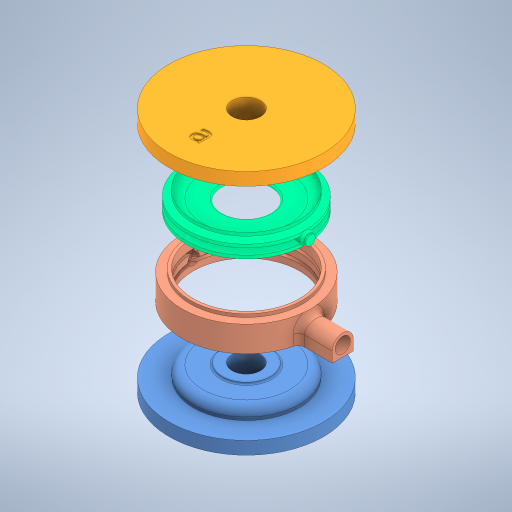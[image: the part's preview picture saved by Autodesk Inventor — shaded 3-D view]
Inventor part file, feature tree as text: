
AUTODESK INVENTOR PART (.ipt)
format: ipt  version: 2023.3 (Build 273359000, 359)  size: 1,031,680 bytes
history: native  units: mm
features: other x12, sketch x6, extrude x6, move_body x6, boolean_combine x4, thicken_offset x4, emboss x2, projected_geometry x2, direct_edit x1
ambient origin geometry x8: Origin, YZ Plane, XZ Plane, XY Plane, X Axis, Y Axis, Z Axis, Center Point
bodies: Solid3 (feature_tree), Solid4 (feature_tree), Solid8 (feature_tree), Solid9 (feature_tree), Solid1 (feature_tree), Solid1_1 (feature_tree), Solid1_2 (feature_tree), Solid1_3 (feature_tree), Solid1_4 (feature_tree)
feature tree (43):
  other  "Sealingring_holder.ipt"
  other  "Sealingring.ipt"
  sketch  "Sketch1"  dims[d0=10.0mm d1=10.0mm]
  extrude  "Extrusion1"  Depth=10.0mm
  boolean_combine  "Combine1"
  sketch  "Sketch2"  dims[d2=8.0mm d3=0.0mm d4=8.8mm]
  extrude  "Extrusion2"  Depth=8.8mm
  thicken_offset  "Thicken1"
  extrude  "Extrusion3"  Depth=0.1mm
  boolean_combine  "Combine2"
  extrude  "Extrusion4"  Depth=8.0mm TaperAngle=0.0deg
  thicken_offset  "Thicken2"
  thicken_offset  "Thicken3"
  thicken_offset  "Thicken4"
  emboss  "Emboss1"
  emboss  "Emboss2"
  extrude  "Extrusion5"  Depth=10.0mm
  boolean_combine  "Combine3"
  extrude  "Extrusion6"  Depth=10.0mm
  boolean_combine  "Combine4"
  direct_edit  "Direct Edit1"
  other  "Solid1::Sealingring_holder.ipt"
  other  "TaggingFeature1"
  other  "Solid1::Sealingring.ipt"
  other  "TaggingFeature2"
  other  "Solid1::Sealingring_holder.ipt_1"
  other  "TaggingFeature3"
  other  "Solid1::Sealingring.ipt_1"
  other  "TaggingFeature4"
  sketch  "Sketch3"  dims[d5=1.5mm d6=0.0mm d7=0.1mm]
  sketch  "Sketch4"  dims[d8=0.1mm d9=8.0mm d10=0.0mm]
  other  "Solid1::Sealingring_holder.ipt_2"
  other  "TaggingFeature5"
  sketch  "Sketch5"  dims[d11=10.0mm d12=10.0mm]
  projected_geometry  "Projected Loop1"
  projected_geometry  "Projected Loop2"
  sketch  "Sketch6"  dims[d13=3.0mm d14=-1.22173mm d15=0.341181mm d16=0.35mm d17=0.1mm d18=0.1mm d19=4.0mm d20=4.0mm d21=4.0mm d22=4.0mm d23=0.3mm d24=0.0mm d25=0.3mm d26=0.0mm d27=10.0mm d28=10.0mm d29=0.0mm d30=6.0mm d31=0.0mm d32=0.0mm d33=0.0mm d34=38.0mm d35=0.0mm d36=0.0mm d37=30.25mm d38=0.0mm d39=0.0mm d40=-14.75mm d41=0.0mm d42=0.0mm d43=8.5mm d44=0.0mm d45=0.0mm d46=5.0mm d47=0.0mm d48=0.0mm d49=-12.75mm]
  move_body  "Move1"
  move_body  "Move2"
  move_body  "Move3"
  move_body  "Move4"
  move_body  "Move5"
  move_body  "Move6"
